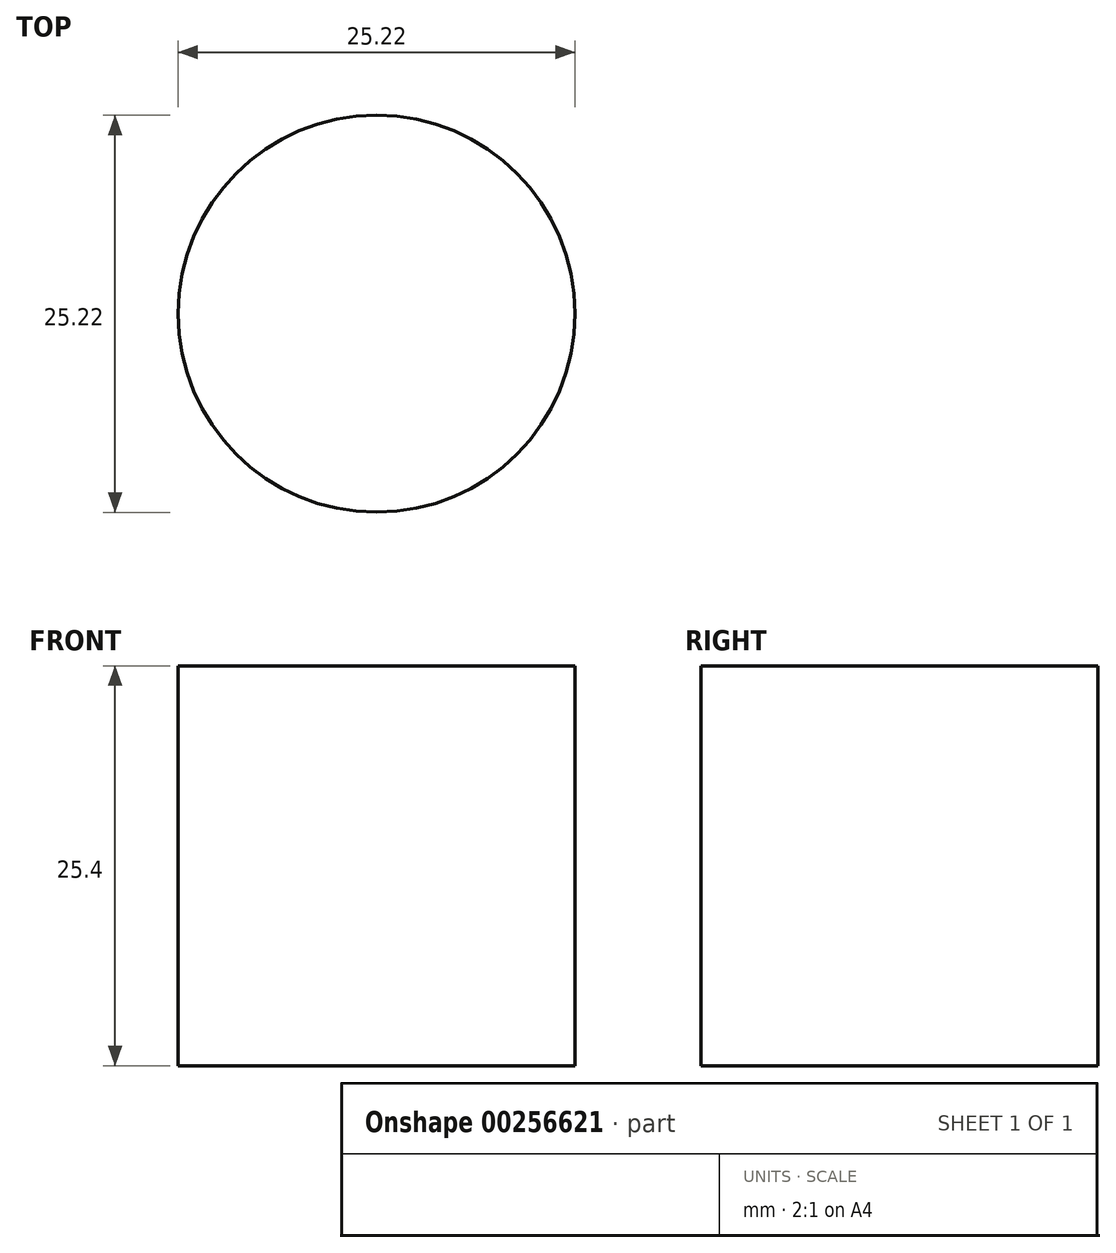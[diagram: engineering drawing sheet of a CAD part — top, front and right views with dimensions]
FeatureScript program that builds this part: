
annotation { "Feature Type Name" : "Feature", "Feature Type Description" : "" }
export const myFeature = defineFeature(function(context is Context, id is Id, definition is map)
    precondition{}
    {
        {
            var Q0;
            Q0=qCreatedBy(makeId("Top.planeOp"),FACE);
            var sketch = newSketch(context, id + "F0", { "sketchPlane" : qUnion([Q0])});
            skCircle(sketch, "E0", {"center": v(0, 0) * mm, "radius": 12.6 * mm});
            skSolve(sketch);
        }
        {
            var Q0;
            Q0=makeQuery(id+"F0.imprint","IMPRINT",FACE,{"disambiguationData":[TD([[makeQuery(id+"F0.imprint","IMPRINT",EDGE,{"derivedFrom":sQuery(id+"F0.wireOp",EDGE,"E0")}),1.0]])]});
            extrude(context, id + "F1", {"entities" : qUnion([Q0]), "depth" : 25.4 * mm});
        }
    });
